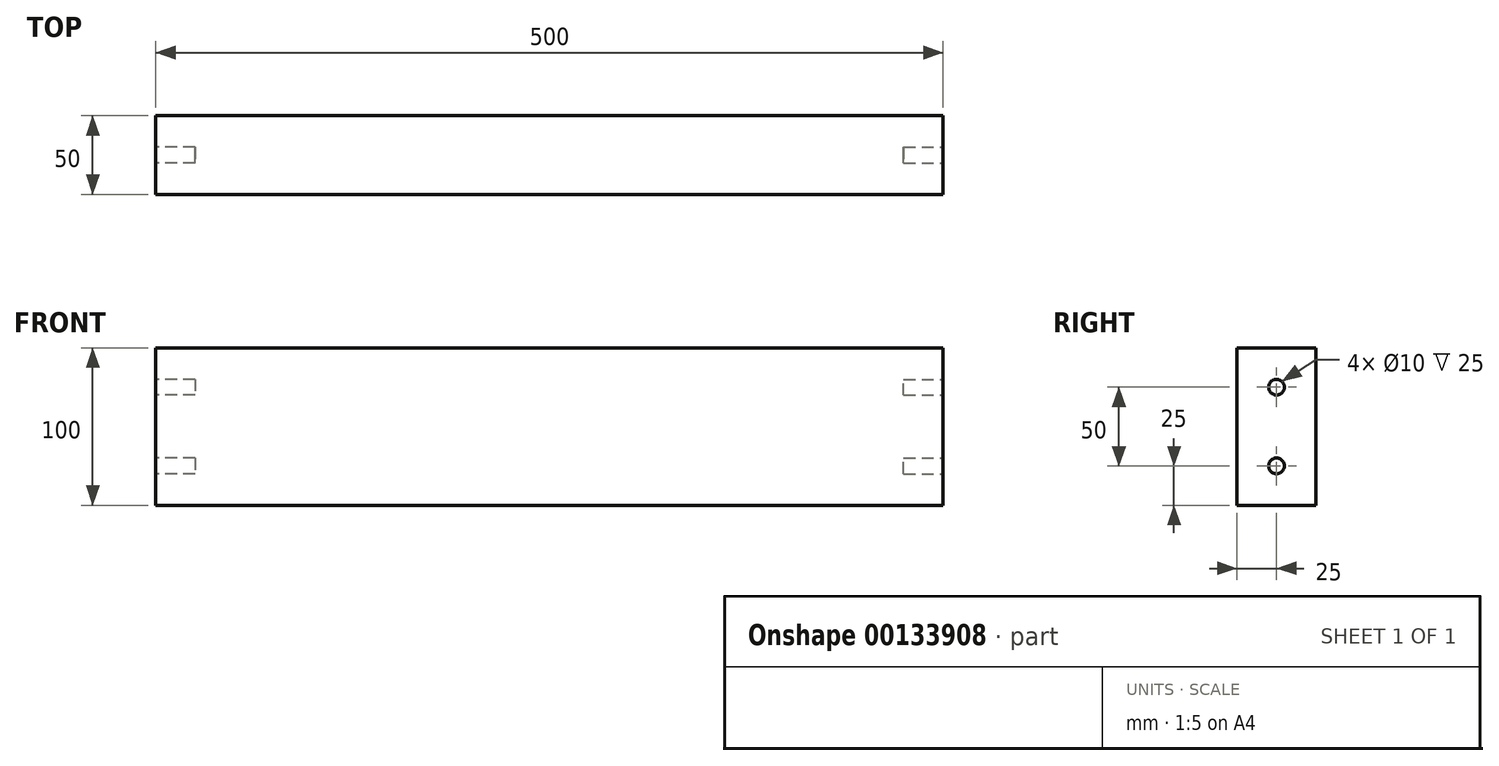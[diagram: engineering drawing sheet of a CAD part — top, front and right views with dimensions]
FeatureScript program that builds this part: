
annotation { "Feature Type Name" : "Feature", "Feature Type Description" : "" }
export const myFeature = defineFeature(function(context is Context, id is Id, definition is map)
    precondition{}
    {
        {
            var Q0;
            Q0=qCreatedBy(makeId("Front.planeOp"),FACE);
            var sketch = newSketch(context, id + "F0", { "sketchPlane" : qUnion([Q0])});
            skLineSegment(sketch, "E0.bottom", {"start": v(250, -50) * mm, "end": v(-250, -50) * mm});
            skLineSegment(sketch, "E0.top", {"start": v(250, 50) * mm, "end": v(-250, 50) * mm});
            skLineSegment(sketch, "E0.left", {"start": v(250, -50) * mm, "end": v(250, 50) * mm});
            skLineSegment(sketch, "E0.right", {"start": v(-250, -50) * mm, "end": v(-250, 50) * mm});
            skPoint(sketch, "E0.middle", {"position": v(0, 0) * mm});
            skSolve(sketch);
        }
        {
            var Q0;
            Q0=makeQuery(id+"F0.imprint","IMPRINT",FACE,{"disambiguationData":[TD([[makeQuery(id+"F0.imprint","IMPRINT",EDGE,{"derivedFrom":sQuery(id+"F0.wireOp",EDGE,"E0.bottom")}),-1.0]])]});
            extrude(context, id + "F1", {"entities" : qUnion([Q0]), "depth" : 50 * mm});
        }
        {
            var Q0;
            Q0=makeQuery(id+"F1.opExtrude","SWEPT_FACE",FACE,{"disambiguationData":[OSD([sQuery(id+"F0.wireOp",EDGE,"E0.right")])]});
            var sketch = newSketch(context, id + "F2", { "sketchPlane" : qUnion([Q0])});
            skCircle(sketch, "E1", {"center": v(25, 25) * mm, "radius": 5 * mm});
            skPoint(sketch, "E1.centerSnap0", {"position": v(25, 50) * mm});
            skCircle(sketch, "E2", {"center": v(25, -25) * mm, "radius": 5 * mm});
            skPoint(sketch, "E2.centerSnap0", {"position": v(25, -50) * mm});
            skSolve(sketch);
        }
        {
            var Q0;
            Q0=makeQuery(id+"F1.opExtrude","SWEPT_FACE",FACE,{"disambiguationData":[OSD([sQuery(id+"F0.wireOp",EDGE,"E0.left")])]});
            var sketch = newSketch(context, id + "F3", { "sketchPlane" : qUnion([Q0])});
            skCircle(sketch, "E3", {"center": v(-25, 25) * mm, "radius": 5 * mm});
            skPoint(sketch, "E3.centerSnap0", {"position": v(-25, 50) * mm});
            skCircle(sketch, "E4", {"center": v(-25, -25) * mm, "radius": 5 * mm});
            skPoint(sketch, "E4.centerSnap0", {"position": v(-25, -50) * mm});
            skSolve(sketch);
        }
        {
            var Q0;
            Q0=makeQuery(id+"F3.imprint","IMPRINT",FACE,{"disambiguationData":[TD([[makeQuery(id+"F3.imprint","IMPRINT",EDGE,{"derivedFrom":sQuery(id+"F3.wireOp",EDGE,"E3")}),1.0]])]});
            var Q1;
            Q1=makeQuery(id+"F3.imprint","IMPRINT",FACE,{"disambiguationData":[TD([[makeQuery(id+"F3.imprint","IMPRINT",EDGE,{"derivedFrom":sQuery(id+"F3.wireOp",EDGE,"E4")}),1.0]])]});
            extrude(context, id + "F4", {"entities" : qUnion([Q0, Q1]), "operationType" : NewBodyOperationType.REMOVE, "oppositeDirection" : true, "depth" : 25 * mm});
        }
        {
            var Q0;
            Q0=makeQuery(id+"F2.imprint","IMPRINT",FACE,{"disambiguationData":[TD([[makeQuery(id+"F2.imprint","IMPRINT",EDGE,{"derivedFrom":sQuery(id+"F2.wireOp",EDGE,"E1")}),1.0]])]});
            var Q1;
            Q1=makeQuery(id+"F2.imprint","IMPRINT",FACE,{"disambiguationData":[TD([[makeQuery(id+"F2.imprint","IMPRINT",EDGE,{"derivedFrom":sQuery(id+"F2.wireOp",EDGE,"E2")}),1.0]])]});
            extrude(context, id + "F5", {"entities" : qUnion([Q0, Q1]), "operationType" : NewBodyOperationType.REMOVE, "oppositeDirection" : true, "depth" : 25 * mm});
        }
    });
